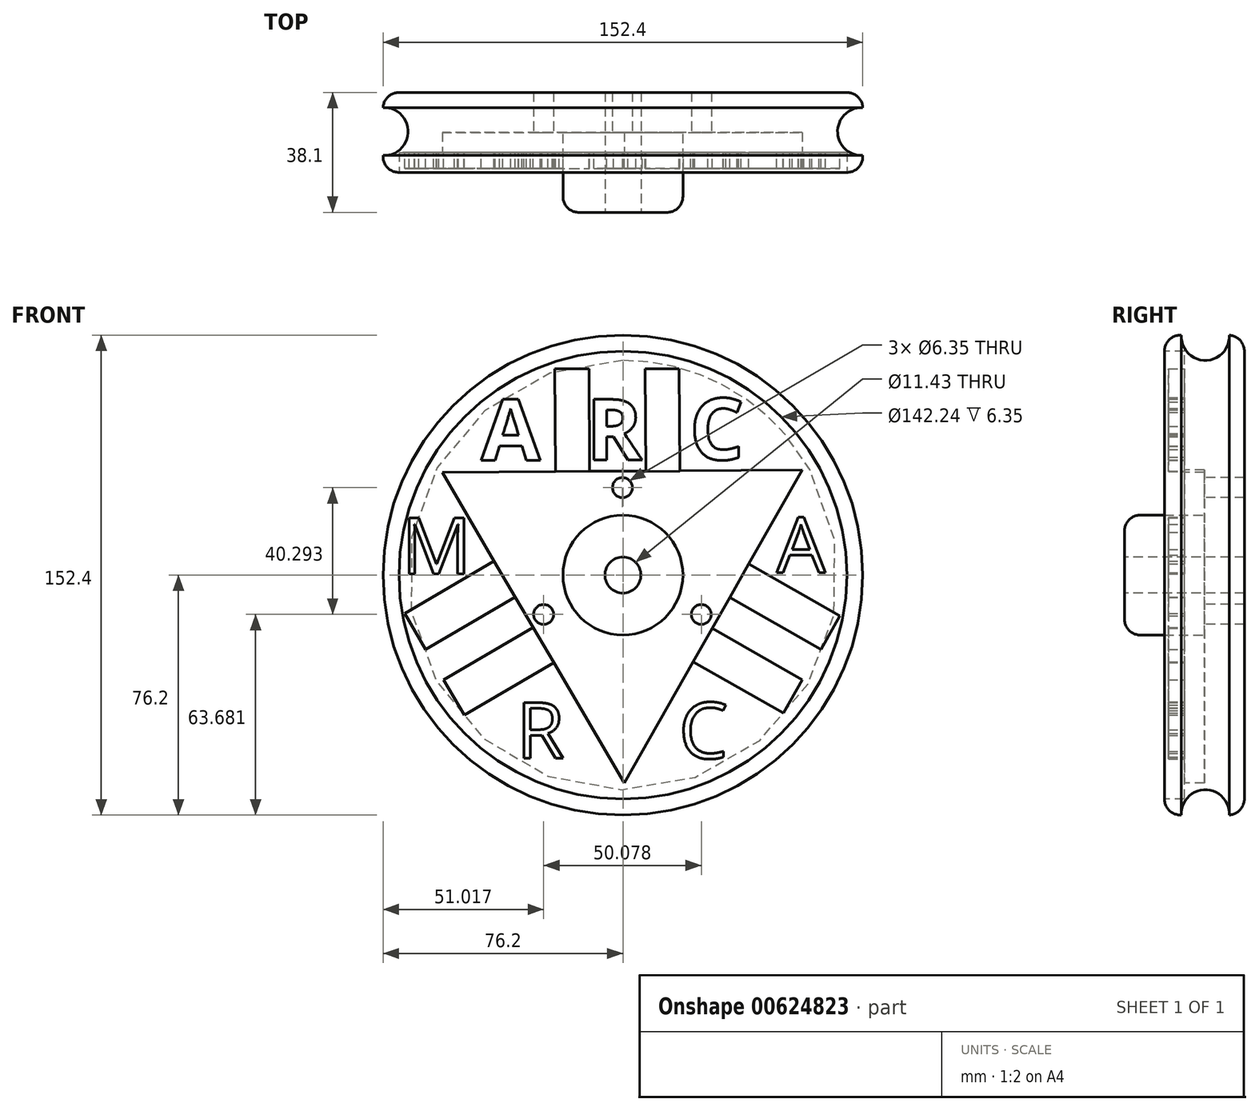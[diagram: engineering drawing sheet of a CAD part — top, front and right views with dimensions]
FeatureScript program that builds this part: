
annotation { "Feature Type Name" : "Feature", "Feature Type Description" : "" }
export const myFeature = defineFeature(function(context is Context, id is Id, definition is map)
    precondition{}
    {
        {
            var Q0;
            Q0=qCreatedBy(makeId("Front.planeOp"),FACE);
            var sketch = newSketch(context, id + "F0", { "sketchPlane" : qUnion([Q0])});
            skCircle(sketch, "E0", {"center": v(0, 0) * mm, "radius": 76.2 * mm});
            skSolve(sketch);
        }
        {
            var Q0;
            Q0 = qSketchRegion(id + "F0", true);
            extrude(context, id + "F1", {"entities" : qUnion([Q0]), "depth" : 25.4 * mm, "offsetDistance" : 25.4 * mm});
        }
        {
            var Q0;
            Q0=makeQuery(id+"F1.opExtrude","CAP_FACE",FACE,{"disambiguationData":[OSD([sQuery(id+"F0.wireOp",EDGE,"E0")])],"isStart":false});
            var sketch = newSketch(context, id + "F2", { "sketchPlane" : qUnion([Q0])});
            skCircle(sketch, "E1", {"center": v(0, 0) * mm, "radius": 19.05 * mm});
            skSolve(sketch);
        }
        {
            var Q0;
            Q0 = qSketchRegion(id + "F2", true);
            extrude(context, id + "F3", {"entities" : qUnion([Q0]), "operationType" : NewBodyOperationType.ADD, "depth" : 12.7 * mm, "offsetDistance" : 25.4 * mm});
        }
        {
            var Q0;
            Q0=makeQuery(id+"F3.opExtrude","CAP_FACE",FACE,{"disambiguationData":[OSD([sQuery(id+"F2.wireOp",EDGE,"E1")])],"isStart":false});
            var sketch = newSketch(context, id + "F4", { "sketchPlane" : qUnion([Q0])});
            skPoint(sketch, "E2", {"position": v(0, 0) * mm});
            skSolve(sketch);
        }
        {
            var Q0;
            Q0=sQuery(id+"F4.wireOp",VERTEX,"E2");
            var Q1;
            Q1=makeQuery(id+"F1.opExtrude","SWEPT_BODY",BODY,{"disambiguationData":[OSD([sQuery(id+"F0.wireOp",EDGE,"E0")])]});
            hole(context, id + "F5", {"style" : HoleStyle.SIMPLE, "endStyle" : HoleEndStyle.THROUGH, "holeDiameter" : 11.43 * mm, "majorDiameter" : 6.35 * mm, "isTappedThrough" : true, "tappedDepth" : 12.7 * mm, "tapClearance" : 3, "locations" : qUnion([Q0]), "scope" : qUnion([Q1])});
        }
        {
            var Q0;
            Q0=makeQuery(id+"F1.opExtrude","CAP_EDGE",EDGE,{"disambiguationData":[OSD([sQuery(id+"F0.wireOp",EDGE,"E0")])],"isStart":false});
            var Q1;
            Q1=makeQuery(id+"F3.opExtrude","CAP_EDGE",EDGE,{"disambiguationData":[OSD([sQuery(id+"F2.wireOp",EDGE,"E1")])],"isStart":false});
            var Q2;
            Q2=makeQuery(id+"F1.opExtrude","SWEPT_FACE",FACE,{"disambiguationData":[OSD([sQuery(id+"F0.wireOp",EDGE,"E0")])]});
            fillet(context, id + "F6", {"entities" : qUnion([Q0, Q1, Q2]), "radius" : 5.08 * mm, "tangentPropagation" : true, "allowEdgeOverflow" : false});
        }
        {
            var Q0;
            Q0=qCreatedBy(makeId("Right.planeOp"),FACE);
            var sketch = newSketch(context, id + "F7", { "sketchPlane" : qUnion([Q0])});
            skCircle(sketch, "E3", {"center": v(-12.4, 75.8) * mm, "radius": 7.62 * mm});
            skSolve(sketch);
        }
        {
            var Q0;
            Q0 = qSketchRegion(id + "F7", true);
            var Q1;
            Q1=makeQuery(id+"F1.opExtrude","SWEPT_FACE",FACE,{"disambiguationData":[OSD([sQuery(id+"F0.wireOp",EDGE,"E0")])]});
            revolve(context, id + "F8", {"operationType" : NewBodyOperationType.REMOVE, "entities" : qUnion([Q0]), "axis" : qUnion([Q1]), "revolveType" : RevolveType.FULL, "oppositeDirection" : true});
        }
        {
            var Q0;
            Q0=makeQuery(id+"F1.opExtrude","CAP_FACE",FACE,{"disambiguationData":[OSD([sQuery(id+"F0.wireOp",EDGE,"E0")])],"isStart":false});
            extrude(context, id + "F9", {"entities" : qUnion([Q0]), "operationType" : NewBodyOperationType.REMOVE, "oppositeDirection" : true, "depth" : 6.35 * mm, "offsetDistance" : 25.4 * mm});
        }
        {
            var Q0;
            Q0=makeQuery(id+"F9.boolean.opBoolean","COPY",FACE,{"derivedFrom":makeQuery(id+"F9.opExtrude","CAP_FACE",FACE,{"disambiguationData":[OSD([sQuery(id+"F0.wireOp",EDGE,"E0")])],"isStart":false})});
            var sketch = newSketch(context, id + "F10", { "sketchPlane" : qUnion([Q0])});
            skCircle(sketch, "E4.cCircle", {"center": v(0, 0) * mm, "radius": 33.02 * mm, "construction": true});
            skLineSegment(sketch, "E4.0", {"start": v(56.98, 33.38) * mm, "end": v(0.42, -66.04) * mm});
            skLineSegment(sketch, "E4.1", {"start": v(0.42, -66.04) * mm, "end": v(-57.4, 32.66) * mm});
            skLineSegment(sketch, "E4.2", {"start": v(-57.4, 32.66) * mm, "end": v(56.98, 33.38) * mm});
            skPoint(sketch, "E4.0.midPoint", {"position": v(28.7, -16.33) * mm});
            skSolve(sketch);
        }
        {
            var Q0;
            Q0=makeQuery(id+"F10.imprint","IMPRINT",FACE,{"disambiguationData":[TD([[makeQuery(id+"F10.imprint","IMPRINT",EDGE,{"derivedFrom":sQuery(id+"F10.wireOp",EDGE,"E4.0")}),-1.0]])]});
            extrude(context, id + "F11", {"entities" : qUnion([Q0]), "operationType" : NewBodyOperationType.REMOVE, "oppositeDirection" : true, "depth" : 6.35 * mm, "offsetDistance" : 25.4 * mm});
        }
        {
            var Q0;
            Q0=makeQuery(id+"F11.boolean.opBoolean","COPY",FACE,{"derivedFrom":makeQuery(id+"F11.opExtrude","CAP_FACE",FACE,{"disambiguationData":[OSD([sQuery(id+"F0.wireOp",EDGE,"E0"),sQuery(id+"F2.wireOp",EDGE,"E1"),sQuery(id+"F10.wireOp",EDGE,"E4.0"),sQuery(id+"F10.wireOp",EDGE,"E4.1"),sQuery(id+"F10.wireOp",EDGE,"E4.2")])],"isStart":false})});
            var sketch = newSketch(context, id + "F12", { "sketchPlane" : qUnion([Q0])});
            skPoint(sketch, "E5", {"position": v(24.9, -12.52) * mm});
            skPoint(sketch, "E6", {"position": v(-25.18, -12.52) * mm});
            skPoint(sketch, "E7", {"position": v(-0.14, 27.77) * mm});
            skSolve(sketch);
        }
        {
            var Q0;
            Q0=sQuery(id+"F12.wireOp",VERTEX,"E6");
            var Q1;
            Q1=sQuery(id+"F12.wireOp",VERTEX,"E5");
            var Q2;
            Q2=sQuery(id+"F12.wireOp",VERTEX,"E7");
            var Q3;
            Q3=makeQuery(id+"F1.opExtrude","SWEPT_BODY",BODY,{"disambiguationData":[OSD([sQuery(id+"F0.wireOp",EDGE,"E0")])]});
            hole(context, id + "F13", {"style" : HoleStyle.SIMPLE, "endStyle" : HoleEndStyle.THROUGH, "holeDiameter" : 6.35 * mm, "majorDiameter" : 6.35 * mm, "isTappedThrough" : true, "tappedDepth" : 12.7 * mm, "tapClearance" : 3, "locations" : qUnion([Q0, Q1, Q2]), "scope" : qUnion([Q3])});
        }
        {
            var Q0;
            Q0=makeQuery(id+"F9.boolean.opBoolean","COPY",FACE,{"derivedFrom":makeQuery(id+"F9.opExtrude","CAP_FACE",FACE,{"disambiguationData":[OSD([sQuery(id+"F0.wireOp",EDGE,"E0")])],"isStart":false})});
            var sketch = newSketch(context, id + "F14", { "sketchPlane" : qUnion([Q0])});
            skLineSegment(sketch, "E8", {"start": v(-21.44, 32.89) * mm, "end": v(-21.64, 65.47) * mm});
            skLineSegment(sketch, "E9", {"start": v(-21.64, 65.47) * mm, "end": v(-10.8, 65.54) * mm});
            skLineSegment(sketch, "E10", {"start": v(-10.8, 65.54) * mm, "end": v(-10.6, 32.95) * mm});
            skLineSegment(sketch, "E11", {"start": v(-10.6, 32.95) * mm, "end": v(-21.44, 32.89) * mm});
            skLineSegment(sketch, "E12", {"start": v(7.05, 65.54) * mm, "end": v(7.26, 32.89) * mm});
            skLineSegment(sketch, "E13", {"start": v(7.26, 32.89) * mm, "end": v(18.1, 32.95) * mm});
            skLineSegment(sketch, "E14", {"start": v(18.1, 32.95) * mm, "end": v(17.9, 65.54) * mm});
            skLineSegment(sketch, "E15", {"start": v(17.9, 65.54) * mm, "end": v(7.05, 65.54) * mm});
            skLineSegment(sketch, "E16", {"start": v(22.3, -27.57) * mm, "end": v(50.94, -43.86) * mm});
            skLineSegment(sketch, "E17", {"start": v(50.94, -43.86) * mm, "end": v(56.98, -33.24) * mm});
            skLineSegment(sketch, "E18", {"start": v(56.98, -33.24) * mm, "end": v(28.35, -16.94) * mm});
            skLineSegment(sketch, "E19", {"start": v(28.35, -16.94) * mm, "end": v(22.3, -27.57) * mm});
            skLineSegment(sketch, "E20", {"start": v(33.94, -7.12) * mm, "end": v(62.89, -23.6) * mm});
            skLineSegment(sketch, "E21", {"start": v(62.89, -23.6) * mm, "end": v(68.93, -12.97) * mm});
            skLineSegment(sketch, "E22", {"start": v(68.93, -12.97) * mm, "end": v(39.98, 3.5) * mm});
            skLineSegment(sketch, "E23", {"start": v(39.98, 3.5) * mm, "end": v(33.94, -7.12) * mm});
            skLineSegment(sketch, "E24", {"start": v(-34.2, -6.94) * mm, "end": v(-62.63, -23.6) * mm});
            skLineSegment(sketch, "E25", {"start": v(-62.63, -23.6) * mm, "end": v(-69.32, -12.16) * mm});
            skLineSegment(sketch, "E26", {"start": v(-69.32, -12.16) * mm, "end": v(-40.9, 4.49) * mm});
            skLineSegment(sketch, "E27", {"start": v(-40.9, 4.49) * mm, "end": v(-34.2, -6.94) * mm});
            skLineSegment(sketch, "E28", {"start": v(-28.5, -16.69) * mm, "end": v(-56.92, -33.34) * mm});
            skLineSegment(sketch, "E29", {"start": v(-56.92, -33.34) * mm, "end": v(-50.39, -44.49) * mm});
            skLineSegment(sketch, "E30", {"start": v(-50.39, -44.49) * mm, "end": v(-21.96, -27.84) * mm});
            skLineSegment(sketch, "E31", {"start": v(-21.96, -27.84) * mm, "end": v(-28.5, -16.69) * mm});
            skSolve(sketch);
        }
        {
            var Q0;
            Q0 = qSketchRegion(id + "F14", true);
            extrude(context, id + "F15", {"entities" : qUnion([Q0]), "operationType" : NewBodyOperationType.ADD, "depth" : 5.08 * mm, "offsetDistance" : 25.4 * mm});
        }
        {
            var Q0;
            Q0=makeQuery(id+"F11.boolean.opBoolean","COPY",FACE,{"derivedFrom":makeQuery(id+"F11.opExtrude","CAP_FACE",FACE,{"disambiguationData":[OSD([sQuery(id+"F0.wireOp",EDGE,"E0"),sQuery(id+"F2.wireOp",EDGE,"E1"),sQuery(id+"F10.wireOp",EDGE,"E4.0"),sQuery(id+"F10.wireOp",EDGE,"E4.1"),sQuery(id+"F10.wireOp",EDGE,"E4.2")])],"isStart":false})});
            var sketch = newSketch(context, id + "F16", { "sketchPlane" : qUnion([Q0])});
            skCircle(sketch, "E32.cCircle", {"center": v(0, 0) * mm, "radius": 22.86 * mm, "construction": true});
            skLineSegment(sketch, "E32.0", {"start": v(39.6, 22.86) * mm, "end": v(0, -45.72) * mm});
            skLineSegment(sketch, "E32.1", {"start": v(0, -45.72) * mm, "end": v(-39.6, 22.86) * mm});
            skLineSegment(sketch, "E32.2", {"start": v(-39.6, 22.86) * mm, "end": v(39.6, 22.86) * mm});
            skPoint(sketch, "E32.0.midPoint", {"position": v(19.8, -11.43) * mm});
            skLineSegment(sketch, "E33", {"start": v(0, -45.72) * mm, "end": v(0, -19.05) * mm});
            skLineSegment(sketch, "E34", {"start": v(0, -19.05) * mm, "end": v(0, -45.72) * mm});
            skLineSegment(sketch, "E35", {"start": v(39.6, 22.86) * mm, "end": v(16.5, 9.53) * mm});
            skLineSegment(sketch, "E36", {"start": v(16.5, 9.53) * mm, "end": v(39.6, 22.86) * mm});
            skLineSegment(sketch, "E37", {"start": v(-39.6, 22.86) * mm, "end": v(-16.5, 9.52) * mm});
            skLineSegment(sketch, "E38", {"start": v(-16.5, 9.52) * mm, "end": v(-39.6, 22.86) * mm});
            skSolve(sketch);
        }
        {
            var Q0;
            Q0=makeQuery(id+"F16.imprint","IMPRINT",FACE,{"disambiguationData":[TD([[makeQuery(id+"F16.imprint","IMPRINT",EDGE,{"derivedFrom":sQuery(id+"F16.wireOp",EDGE,"E32.0")}),-1.0]])]});
            var Q1;
            Q1=sQuery(id+"F16.wireOp",EDGE,"E32.1");
            var Q2;
            Q2=sQuery(id+"F16.wireOp",EDGE,"E32.2");
            var Q3;
            Q3=sQuery(id+"F16.wireOp",EDGE,"E32.0");
            extrude(context, id + "F17", {"entities" : qUnion([Q0]), "bodyType" : ToolBodyType.SURFACE, "surfaceEntities" : qUnion([Q1, Q2, Q3]), "depth" : 7.62 * mm, "offsetDistance" : 25.4 * mm});
        }
        {
            var Q0;
            Q0=sQuery(id+"F16.wireOp",EDGE,"E38");
            extrude(context, id + "F18", {"bodyType" : ToolBodyType.SURFACE, "surfaceEntities" : qUnion([Q0]), "depth" : 7.62 * mm, "offsetDistance" : 25.4 * mm});
        }
        {
            var Q0;
            Q0=sQuery(id+"F16.wireOp",EDGE,"E36");
            extrude(context, id + "F19", {"bodyType" : ToolBodyType.SURFACE, "surfaceEntities" : qUnion([Q0]), "depth" : 7.62 * mm, "offsetDistance" : 25.4 * mm});
        }
        {
            var Q0;
            Q0=sQuery(id+"F16.wireOp",EDGE,"E34");
            extrude(context, id + "F20", {"bodyType" : ToolBodyType.SURFACE, "surfaceEntities" : qUnion([Q0]), "depth" : 7.62 * mm, "offsetDistance" : 25.4 * mm});
        }
        {
            var Q0;
            Q0=makeQuery(id+"F9.boolean.opBoolean","COPY",FACE,{"derivedFrom":makeQuery(id+"F9.opExtrude","CAP_FACE",FACE,{"disambiguationData":[OSD([sQuery(id+"F0.wireOp",EDGE,"E0")])],"isStart":false})});
            var sketch = newSketch(context, id + "F21", { "sketchPlane" : qUnion([Q0])});
            skText(sketch, "E39", { "text": "M", "fontName": "OpenSans-Regular.ttf"});
            skText(sketch, "E40", { "text": "A", "fontName": "OpenSans-Regular.ttf"});
            skPoint(sketch, "E40.firstSnap0", {"position": v(48.48, 18.44) * mm});
            skText(sketch, "E41", { "text": "R", "fontName": "OpenSans-Regular.ttf"});
            skText(sketch, "E42", { "text": "C", "fontName": "OpenSans-Regular.ttf"});
            skText(sketch, "E43", { "text": "A", "fontName": "OpenSans-Bold.ttf"});
            skText(sketch, "E44", { "text": "C", "fontName": "OpenSans-Bold.ttf"});
            skText(sketch, "E45", { "text": "R", "fontName": "OpenSans-Bold.ttf"});
            const initialGuessF21  = {"E39": [-0.07037, 0.00043, 1, 0, 0.01784], "E40": [0.04878, 0.00072, 1, 0, 0.01772], "E41": [-0.03393, -0.05824, 1, 0, 0.01786], "E42": [0.01775, -0.05824, 1, 0, 0.01786], "E43": [-0.04504, 0.0364, 1, 0, 0.01957], "E44": [0.02115, 0.03667, 1, 0, 0.01958], "E45": [-0.01166, 0.03656, 1, 0, 0.01942]};
            skSetInitialGuess(sketch, initialGuessF21);
            skSolve(sketch);
        }
        {
            var Q0;
            Q0 = qSketchRegion(id + "F21", true);
            extrude(context, id + "F22", {"entities" : qUnion([Q0]), "operationType" : NewBodyOperationType.ADD, "depth" : 5.08 * mm, "offsetDistance" : 25.4 * mm});
        }
        {
            var Q0;
            Q0=makeQuery(id+"F11.boolean.opBoolean","COPY",FACE,{"derivedFrom":makeQuery(id+"F11.opExtrude","CAP_FACE",FACE,{"disambiguationData":[OSD([sQuery(id+"F2.wireOp",EDGE,"E1"),sQuery(id+"F10.wireOp",EDGE,"E4.0"),sQuery(id+"F10.wireOp",EDGE,"E4.1"),sQuery(id+"F10.wireOp",EDGE,"E4.2")])],"isStart":false})});
            var sketch = newSketch(context, id + "F23", { "sketchPlane" : qUnion([Q0])});
            skLineSegment(sketch, "E46", {"start": v(-39.29, 22.88) * mm, "end": v(-57.4, 32.66) * mm});
            skLineSegment(sketch, "E47", {"start": v(-57.4, 32.66) * mm, "end": v(-39.29, 22.88) * mm});
            skLineSegment(sketch, "E48", {"start": v(39.57, 22.88) * mm, "end": v(56.98, 33.38) * mm});
            skLineSegment(sketch, "E49", {"start": v(56.98, 33.38) * mm, "end": v(39.57, 22.88) * mm});
            skLineSegment(sketch, "E50", {"start": v(0.42, -45.62) * mm, "end": v(0.42, -66.04) * mm});
            skLineSegment(sketch, "E51", {"start": v(0.42, -66.04) * mm, "end": v(0.42, -45.62) * mm});
            skSolve(sketch);
        }
        {
            var Q0;
            Q0 = qSketchRegion(id + "F23", true);
            var Q1;
            Q1=sQuery(id+"F23.wireOp",EDGE,"E47");
            var Q2;
            Q2=sQuery(id+"F23.wireOp",EDGE,"E49");
            var Q3;
            Q3=sQuery(id+"F23.wireOp",EDGE,"E51");
            extrude(context, id + "F24", {"entities" : qUnion([Q0]), "bodyType" : ToolBodyType.SURFACE, "surfaceEntities" : qUnion([Q1, Q2, Q3]), "depth" : 7.62 * mm, "offsetDistance" : 25.4 * mm});
        }
    });
